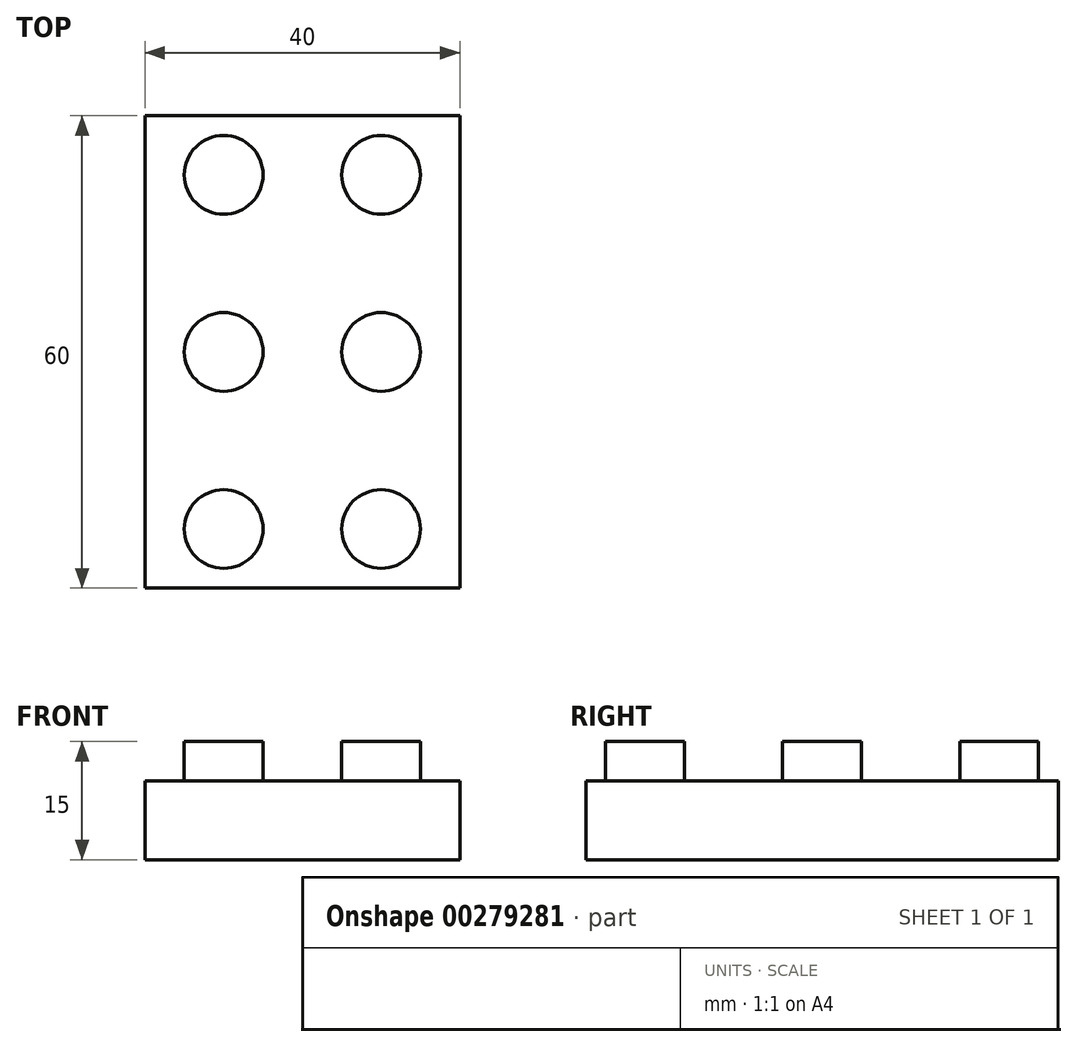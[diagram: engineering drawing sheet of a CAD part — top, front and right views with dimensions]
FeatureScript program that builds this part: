
annotation { "Feature Type Name" : "Feature", "Feature Type Description" : "" }
export const myFeature = defineFeature(function(context is Context, id is Id, definition is map)
    precondition{}
    {
        {
            var Q0;
            Q0=qCreatedBy(makeId("Top.planeOp"),FACE);
            var sketch = newSketch(context, id + "F0", { "sketchPlane" : qUnion([Q0])});
            skLineSegment(sketch, "E0.bottom", {"start": v(-23.82, -23) * mm, "end": v(16.18, -23) * mm});
            skLineSegment(sketch, "E0.top", {"start": v(-23.82, 37) * mm, "end": v(16.18, 37) * mm});
            skLineSegment(sketch, "E0.left", {"start": v(-23.82, -23) * mm, "end": v(-23.82, 37) * mm});
            skLineSegment(sketch, "E0.right", {"start": v(16.18, -23) * mm, "end": v(16.18, 37) * mm});
            skSolve(sketch);
        }
        {
            var Q0;
            Q0=makeQuery(id+"F0.imprint","IMPRINT",FACE,{"disambiguationData":[TD([[makeQuery(id+"F0.imprint","IMPRINT",EDGE,{"derivedFrom":sQuery(id+"F0.wireOp",EDGE,"E0.bottom")}),1.0]])]});
            extrude(context, id + "F1", {"entities" : qUnion([Q0]), "oppositeDirection" : true, "depth" : 10 * mm});
        }
        {
            var Q0;
            Q0=makeQuery(id+"F1.opExtrude","CAP_FACE",FACE,{"disambiguationData":[OSD([sQuery(id+"F0.wireOp",EDGE,"E0.bottom"),sQuery(id+"F0.wireOp",EDGE,"E0.top"),sQuery(id+"F0.wireOp",EDGE,"E0.left"),sQuery(id+"F0.wireOp",EDGE,"E0.right")])],"isStart":true});
            var sketch = newSketch(context, id + "F2", { "sketchPlane" : qUnion([Q0])});
            skCircle(sketch, "E1", {"center": v(-13.82, 29.5) * mm, "radius": 5 * mm});
            skCircle(sketch, "E2", {"center": v(6.18, 29.5) * mm, "radius": 5 * mm});
            skCircle(sketch, "E3", {"center": v(-13.82, -15.5) * mm, "radius": 5 * mm});
            skCircle(sketch, "E4", {"center": v(6.18, 7) * mm, "radius": 5 * mm});
            skCircle(sketch, "E5", {"center": v(-13.82, 7) * mm, "radius": 5 * mm});
            skCircle(sketch, "E6", {"center": v(6.18, -15.5) * mm, "radius": 5 * mm});
            skSolve(sketch);
        }
        {
            var Q0;
            Q0 = qSketchRegion(id + "F2", true);
            extrude(context, id + "F3", {"entities" : qUnion([Q0]), "operationType" : NewBodyOperationType.ADD, "depth" : 5 * mm});
        }
    });
